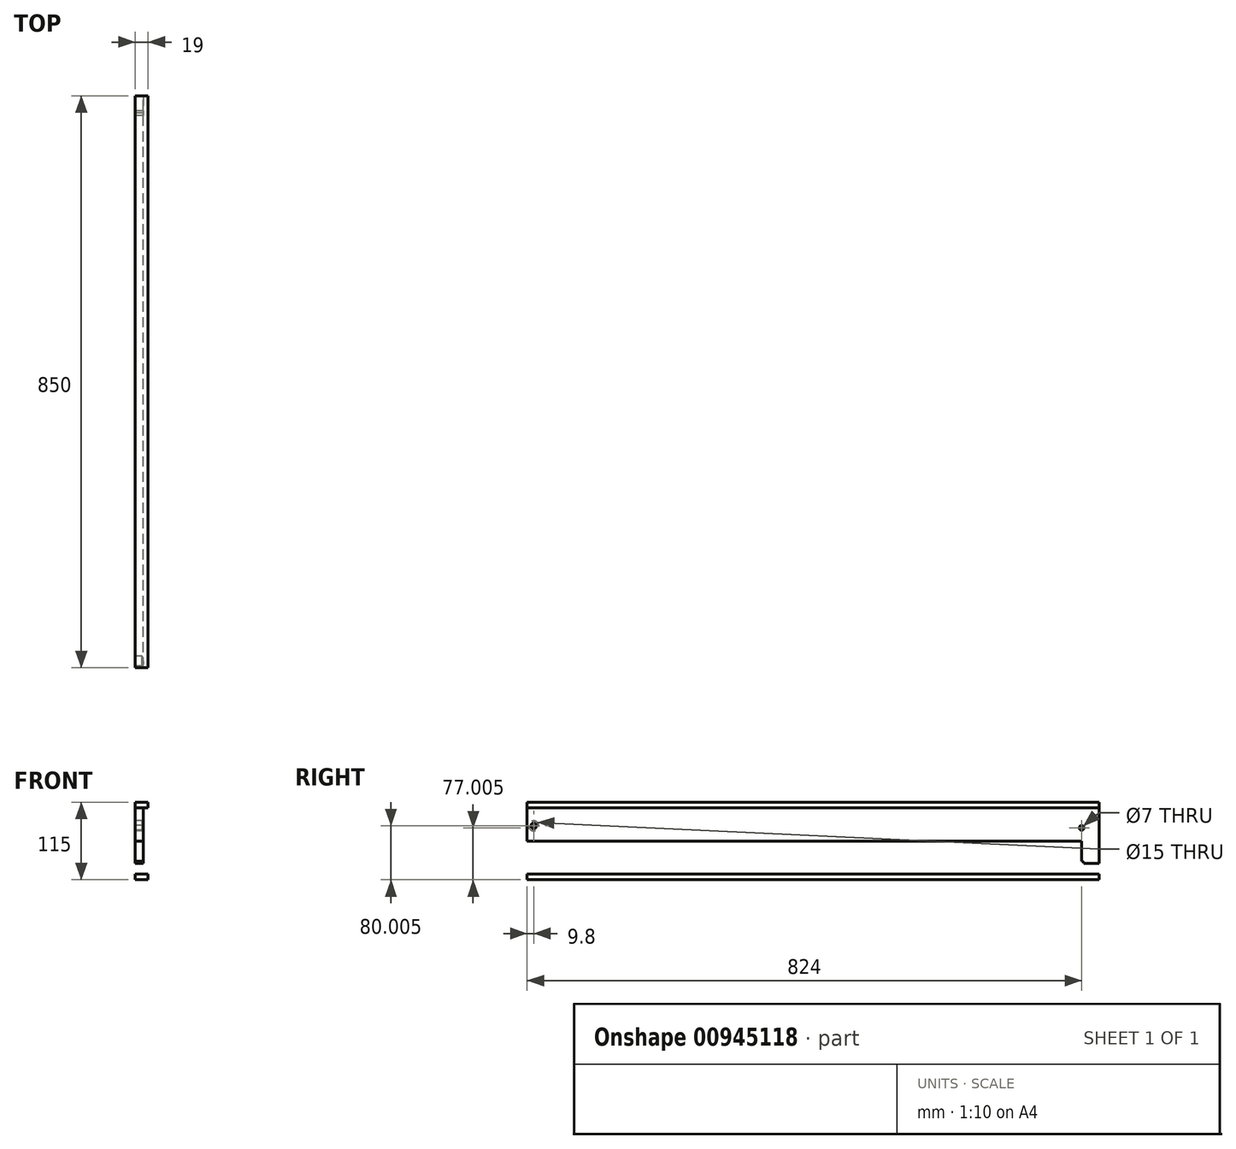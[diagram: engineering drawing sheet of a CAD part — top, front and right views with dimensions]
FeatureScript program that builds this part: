
annotation { "Feature Type Name" : "Feature", "Feature Type Description" : "" }
export const myFeature = defineFeature(function(context is Context, id is Id, definition is map)
    precondition{}
    {
        {
            var Q0;
            Q0=qCreatedBy(makeId("Right.planeOp"),FACE);
            var sketch = newSketch(context, id + "F0", { "sketchPlane" : qUnion([Q0])});
            skLineSegment(sketch, "E0.bottom", {"start": v(843.77, 26.03) * mm, "end": v(-6.23, 26.03) * mm});
            skLineSegment(sketch, "E0.top", {"start": v(843.77, -88.97) * mm, "end": v(-6.23, -88.97) * mm});
            skLineSegment(sketch, "E0.left", {"start": v(843.77, 26.03) * mm, "end": v(843.77, -88.97) * mm});
            skLineSegment(sketch, "E0.right", {"start": v(-6.23, 26.03) * mm, "end": v(-6.23, -88.97) * mm});
            skLineSegment(sketch, "E1", {"start": v(-6.23, 26.03) * mm, "end": v(-6.23, 17.53) * mm});
            skLineSegment(sketch, "E2", {"start": v(-6.23, 17.53) * mm, "end": v(-6.23, -31.47) * mm});
            skLineSegment(sketch, "E3", {"start": v(-6.23, -31.47) * mm, "end": v(843.77, -31.47) * mm});
            skLineSegment(sketch, "E4.MirrorCS", {"start": v(-6.23, -88.97) * mm, "end": v(-6.23, -80.47) * mm});
            skLineSegment(sketch, "E5", {"start": v(-6.23, 17.53) * mm, "end": v(843.77, 17.53) * mm});
            skLineSegment(sketch, "E6.MirrorCS", {"start": v(-6.23, -80.47) * mm, "end": v(843.77, -80.47) * mm});
            skLineSegment(sketch, "E7", {"start": v(843.77, -88.97) * mm, "end": v(843.77, -64.97) * mm});
            skLineSegment(sketch, "E8", {"start": v(843.77, -64.97) * mm, "end": v(817.77, -64.97) * mm});
            skLineSegment(sketch, "E9", {"start": v(817.77, -64.97) * mm, "end": v(817.77, -11.97) * mm});
            skLineSegment(sketch, "E10", {"start": v(-6.23, -88.97) * mm, "end": v(-6.23, -53.97) * mm});
            skLineSegment(sketch, "E11", {"start": v(-6.23, -53.97) * mm, "end": v(3.57, -53.97) * mm});
            skLineSegment(sketch, "E12.MirrorCS", {"start": v(-6.23, -8.97) * mm, "end": v(3.57, -8.97) * mm});
            skSolve(sketch);
        }
        {
            var Q0;
            {var subQ0=sQuery(id+"F0.wireOp",EDGE,"E0.bottom");Q0=makeQuery(id+"F0.imprint","IMPRINT",FACE,{"disambiguationData":[TD([[makeQuery(id+"F0.imprint","IMPRINT",EDGE,{"derivedFrom":subQ0}),1.0]])]});}
            var Q1;
            {var subQ0=sQuery(id+"F0.wireOp",EDGE,"E0.top");Q1=makeQuery(id+"F0.imprint","IMPRINT",FACE,{"disambiguationData":[TD([[makeQuery(id+"F0.imprint","IMPRINT",EDGE,{"derivedFrom":subQ0}),-1.0]])]});}
            extrude(context, id + "F1", {"entities" : qUnion([Q0, Q1]), "depth" : 19 * mm, "offsetDistance" : 25 * mm});
        }
        {
            var Q0;
            Q0=makeQuery(id+"F0.imprint","IMPRINT",FACE,{"disambiguationData":[TD([[makeQuery(id+"F0.imprint","IMPRINT",EDGE,{"derivedFrom":sQuery(id+"F0.wireOp",EDGE,"E2")}),1.0]])]});
            var Q1;
            Q1=makeQuery(id+"F0.imprint","IMPRINT",FACE,{"disambiguationData":[TD([[makeQuery(id+"F0.imprint","IMPRINT",EDGE,{"derivedFrom":sQuery(id+"F0.wireOp",EDGE,"E0.right")}),1.0]])]});
            var Q2;
            {var subQ0=sQuery(id+"F0.wireOp",EDGE,"E8");Q2=makeQuery(id+"F0.imprint","IMPRINT",FACE,{"disambiguationData":[TD([[makeQuery(id+"F0.imprint","IMPRINT",EDGE,{"derivedFrom":subQ0}),-1.0]])]});}
            extrude(context, id + "F2", {"entities" : qUnion([Q0, Q1, Q2]), "depth" : 12 * mm, "offsetDistance" : 25 * mm});
        }
        {
            var Q0;
            Q0=sQuery(id+"F0.wireOp",VERTEX,"E9.end");
            var Q1;
            Q1=sQuery(id+"F0.wireOp",VERTEX,"E8.end");
            var Q2;
            Q2=makeQuery(id+"F2.opExtrude","SWEPT_BODY",BODY,{"disambiguationData":[OSD([sQuery(id+"F0.wireOp",EDGE,"E0.left"),sQuery(id+"F0.wireOp",EDGE,"E0.right"),sQuery(id+"F0.wireOp",EDGE,"E2"),sQuery(id+"F0.wireOp",EDGE,"E5"),sQuery(id+"F0.wireOp",EDGE,"E6.MirrorCS"),sQuery(id+"F0.wireOp",EDGE,"E7")])]});
            hole(context, id + "F3", {"style" : HoleStyle.SIMPLE, "endStyle" : HoleEndStyle.BLIND, "oppositeDirection" : true, "holeDiameter" : 7 * mm, "majorDiameter" : 5 * mm, "holeDepth" : 12 * mm, "isTappedThrough" : true, "tappedDepth" : 12 * mm, "tapClearance" : 3, "locations" : qUnion([Q0, Q1]), "scope" : qUnion([Q2])});
        }
        {
            var Q0;
            Q0=sQuery(id+"F0.wireOp",VERTEX,"E11.end");
            var Q1;
            Q1=sQuery(id+"F0.wireOp",VERTEX,"E12.MirrorCS.end");
            var Q2;
            Q2=makeQuery(id+"F2.opExtrude","SWEPT_BODY",BODY,{"disambiguationData":[OSD([sQuery(id+"F0.wireOp",EDGE,"E0.left"),sQuery(id+"F0.wireOp",EDGE,"E0.right"),sQuery(id+"F0.wireOp",EDGE,"E2"),sQuery(id+"F0.wireOp",EDGE,"E5"),sQuery(id+"F0.wireOp",EDGE,"E6.MirrorCS"),sQuery(id+"F0.wireOp",EDGE,"E7"),sQuery(id+"F0.wireOp",EDGE,"E10")])]});
            hole(context, id + "F4", {"style" : HoleStyle.SIMPLE, "endStyle" : HoleEndStyle.BLIND, "oppositeDirection" : true, "holeDiameter" : 15 * mm, "majorDiameter" : 5 * mm, "holeDepth" : 10 * mm, "isTappedThrough" : true, "tappedDepth" : 12 * mm, "tapClearance" : 3, "locations" : qUnion([Q0, Q1]), "scope" : qUnion([Q2])});
        }
    });
